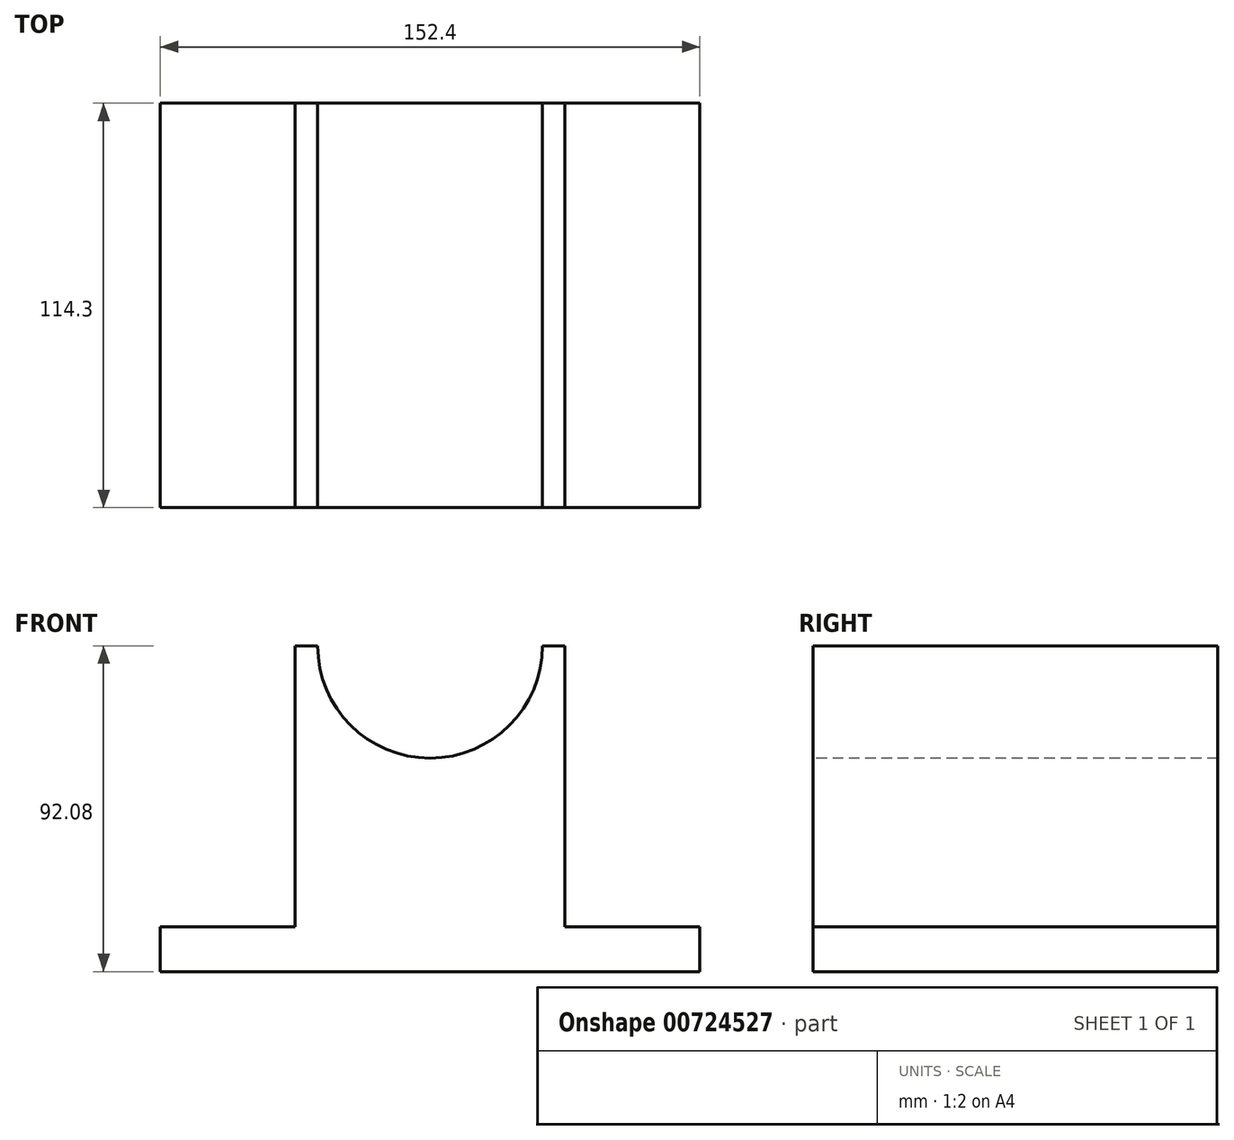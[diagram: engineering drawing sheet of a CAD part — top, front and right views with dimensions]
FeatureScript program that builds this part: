
annotation { "Feature Type Name" : "Feature", "Feature Type Description" : "" }
export const myFeature = defineFeature(function(context is Context, id is Id, definition is map)
    precondition{}
    {
        {
            var Q0;
            Q0=qCreatedBy(makeId("Top.planeOp"),FACE);
            var sketch = newSketch(context, id + "F0", { "sketchPlane" : qUnion([Q0])});
            skLineSegment(sketch, "E0.bottom", {"start": v(76.2, 57.15) * mm, "end": v(-76.2, 57.15) * mm});
            skLineSegment(sketch, "E0.top", {"start": v(76.2, -57.15) * mm, "end": v(-76.2, -57.15) * mm});
            skLineSegment(sketch, "E0.left", {"start": v(76.2, 57.15) * mm, "end": v(76.2, -57.15) * mm});
            skLineSegment(sketch, "E0.right", {"start": v(-76.2, 57.15) * mm, "end": v(-76.2, -57.15) * mm});
            skPoint(sketch, "E0.middle", {"position": v(0, 0) * mm});
            skLineSegment(sketch, "E1", {"start": v(-38.1, 57.15) * mm, "end": v(-38.1, -57.15) * mm});
            skLineSegment(sketch, "E2", {"start": v(38.1, 57.15) * mm, "end": v(38.1, -57.15) * mm});
            skSolve(sketch);
        }
        {
            var Q0;
            {var subQ0=sQuery(id+"F0.wireOp",EDGE,"E0.right");Q0=makeQuery(id+"F0.imprint","IMPRINT",FACE,{"disambiguationData":[TD([[makeQuery(id+"F0.imprint","IMPRINT",EDGE,{"derivedFrom":subQ0}),1.0]])]});}
            var Q1;
            {var subQ0=sQuery(id+"F0.wireOp",EDGE,"E1");Q1=makeQuery(id+"F0.imprint","IMPRINT",FACE,{"disambiguationData":[TD([[makeQuery(id+"F0.imprint","IMPRINT",EDGE,{"derivedFrom":subQ0}),1.0]])]});}
            var Q2;
            {var subQ0=sQuery(id+"F0.wireOp",EDGE,"E0.left");Q2=makeQuery(id+"F0.imprint","IMPRINT",FACE,{"disambiguationData":[TD([[makeQuery(id+"F0.imprint","IMPRINT",EDGE,{"derivedFrom":subQ0}),-1.0]])]});}
            extrude(context, id + "F1", {"entities" : qUnion([Q0, Q1, Q2]), "depth" : 12.7 * mm});
        }
        {
            var Q0;
            {var subQ0=sQuery(id+"F0.wireOp",EDGE,"E1");Q0=makeQuery(id+"F0.imprint","IMPRINT",FACE,{"disambiguationData":[TD([[makeQuery(id+"F0.imprint","IMPRINT",EDGE,{"derivedFrom":subQ0}),1.0]])]});}
            extrude(context, id + "F2", {"entities" : qUnion([Q0]), "operationType" : NewBodyOperationType.ADD, "depth" : 92.07 * mm});
        }
        {
            var Q0;
            {var subQ0=sQuery(id+"F0.wireOp",EDGE,"E0.top");Q0=makeQuery(id+"F2.boolean.opBoolean","MERGE",FACE,{"derivedFrom":[makeQuery(id+"F1.opExtrude","SWEPT_FACE",FACE,{"disambiguationData":[OSD([subQ0])]}),makeQuery(id+"F2.opExtrude","SWEPT_FACE",FACE,{"disambiguationData":[OSD([subQ0])]})]});}
            var sketch = newSketch(context, id + "F3", { "sketchPlane" : qUnion([Q0])});
            skCircle(sketch, "E3", {"center": v(0, 92.08) * mm, "radius": 31.75 * mm});
            skSolve(sketch);
        }
        {
            var Q0;
            Q0=qSketchRegion(id+"F3",true);
            extrude(context, id + "F4", {"entities" : qUnion([Q0]), "operationType" : NewBodyOperationType.REMOVE, "oppositeDirection" : true, "depth" : 114.3 * mm});
        }
    });
